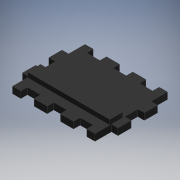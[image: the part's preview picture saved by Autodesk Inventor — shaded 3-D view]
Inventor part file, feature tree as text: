
AUTODESK INVENTOR PART (.ipt)
format: ipt  version: 2019 (Build 230136000, 136)  size: 188,416 bytes
history: native  units: mm
features: extrude x3, sketch x3
ambient origin geometry x8: Origin, YZ Plane, XZ Plane, XY Plane, X Axis, Y Axis, Z Axis, Center Point
bodies: Solid1 (feature_tree)
feature tree (6):
  extrude  "Extrusion1"  Depth=44.0mm
  extrude  "Extrusion2"  Depth=4.0mm
  extrude  "Extrusion3"  Depth=8.0mm
  sketch  "Sketch1"  dims[d0=58.0mm d1=44.0mm]
  sketch  "Sketch2"  dims[d6=4.0mm d7=0.0mm d8=4.0mm]
  sketch  "Sketch3"  dims[d11=8.0mm d12=8.0mm d13=4.0mm d14=4.0mm d15=0.0mm d16=4.0mm d17=8.0mm d18=5.0mm d19=8.0mm d20=3.0mm d21=0.0mm]
